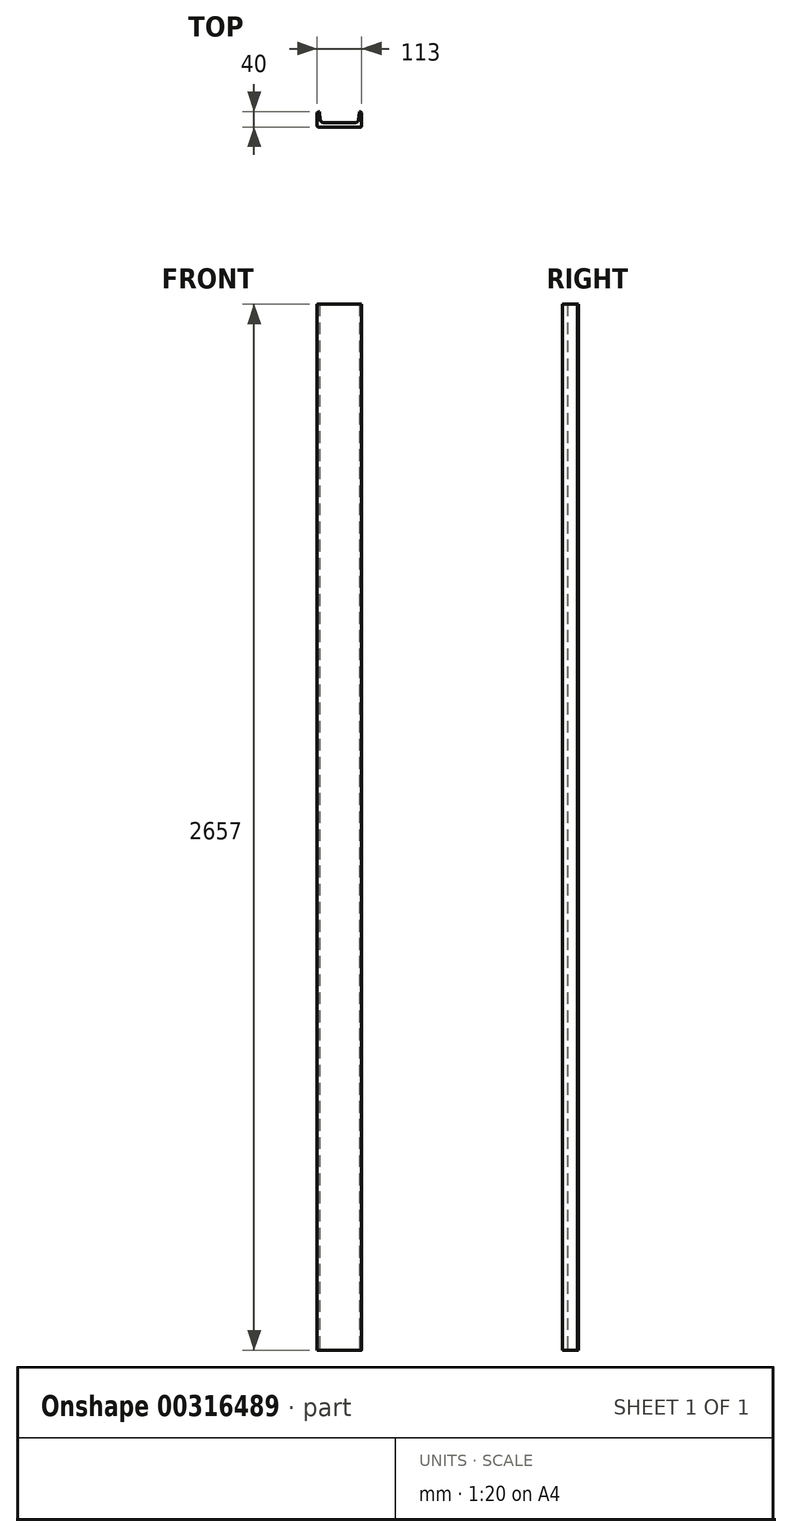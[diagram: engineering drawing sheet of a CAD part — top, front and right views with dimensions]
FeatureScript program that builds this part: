
annotation { "Feature Type Name" : "Feature", "Feature Type Description" : "" }
export const myFeature = defineFeature(function(context is Context, id is Id, definition is map)
    precondition{}
    {
        {
            var Q0;
            Q0=qCreatedBy(makeId("Top.planeOp"),FACE);
            var sketch = newSketch(context, id + "F0", { "sketchPlane" : qUnion([Q0])});
            skLineSegment(sketch, "E0", {"start": v(0, 40) * mm, "end": v(0, 4) * mm});
            skLineSegment(sketch, "E1", {"start": v(4, 0) * mm, "end": v(109, 0) * mm});
            skLineSegment(sketch, "E2", {"start": v(113, 4) * mm, "end": v(113, 40) * mm});
            skLineSegment(sketch, "E3", {"start": v(15.78, 12) * mm, "end": v(97.22, 12) * mm});
            skLineSegment(sketch, "E4", {"start": v(7.81, 19.3) * mm, "end": v(6, 40) * mm});
            skLineSegment(sketch, "E5", {"start": v(105.19, 19.3) * mm, "end": v(107, 40) * mm});
            skLineSegment(sketch, "E6", {"start": v(107, 40) * mm, "end": v(113, 40) * mm});
            skLineSegment(sketch, "E7", {"start": v(6, 40) * mm, "end": v(0, 40) * mm});
            skLineSegment(sketch, "E8", {"start": v(113, 40) * mm, "end": v(113, 37) * mm});
            skLineSegment(sketch, "E9", {"start": v(113, 40) * mm, "end": v(110, 40) * mm});
            skLineSegment(sketch, "E10", {"start": v(110, 40) * mm, "end": v(113, 37) * mm});
            skPoint(sketch, "E11.visualSharp", {"position": v(113, 0) * mm});
            skArc(sketch, "E11.filletArc", {"start": v(109, 0) * mm, "mid": v(111.83, 1.17) * mm, "end": v(113, 4) * mm});
            skPoint(sketch, "E12.visualSharp", {"position": v(0, 0) * mm});
            skArc(sketch, "E12.filletArc", {"start": v(0, 4) * mm, "mid": v(1.17, 1.17) * mm, "end": v(4, 0) * mm});
            skLineSegment(sketch, "E13", {"start": v(56.5, 12) * mm, "end": v(56.5, 55.91) * mm});
            skPoint(sketch, "E14.visualSharp", {"position": v(104.55, 12) * mm});
            skArc(sketch, "E14.filletArc", {"start": v(97.22, 12) * mm, "mid": v(102.62, 14.1) * mm, "end": v(105.19, 19.3) * mm});
            skPoint(sketch, "E15.visualSharp", {"position": v(8.45, 12) * mm});
            skArc(sketch, "E15.filletArc", {"start": v(7.81, 19.3) * mm, "mid": v(10.38, 14.1) * mm, "end": v(15.78, 12) * mm});
            skLineSegment(sketch, "E16", {"start": v(0, 40) * mm, "end": v(3, 40) * mm});
            skLineSegment(sketch, "E17", {"start": v(3, 40) * mm, "end": v(0, 40) * mm});
            skLineSegment(sketch, "E18", {"start": v(3, 40) * mm, "end": v(0, 37) * mm});
            skSolve(sketch);
        }
        {
            var Q0;
            Q0=makeQuery(id+"F0.imprint","IMPRINT",FACE,{"disambiguationData":[TD([[makeQuery(id+"F0.imprint","IMPRINT",EDGE,{"derivedFrom":sQuery(id+"F0.wireOp",EDGE,"E1")}),1.0]])]});
            extrude(context, id + "F1", {"entities" : qUnion([Q0]), "depth" : 2657 * mm});
        }
    });
